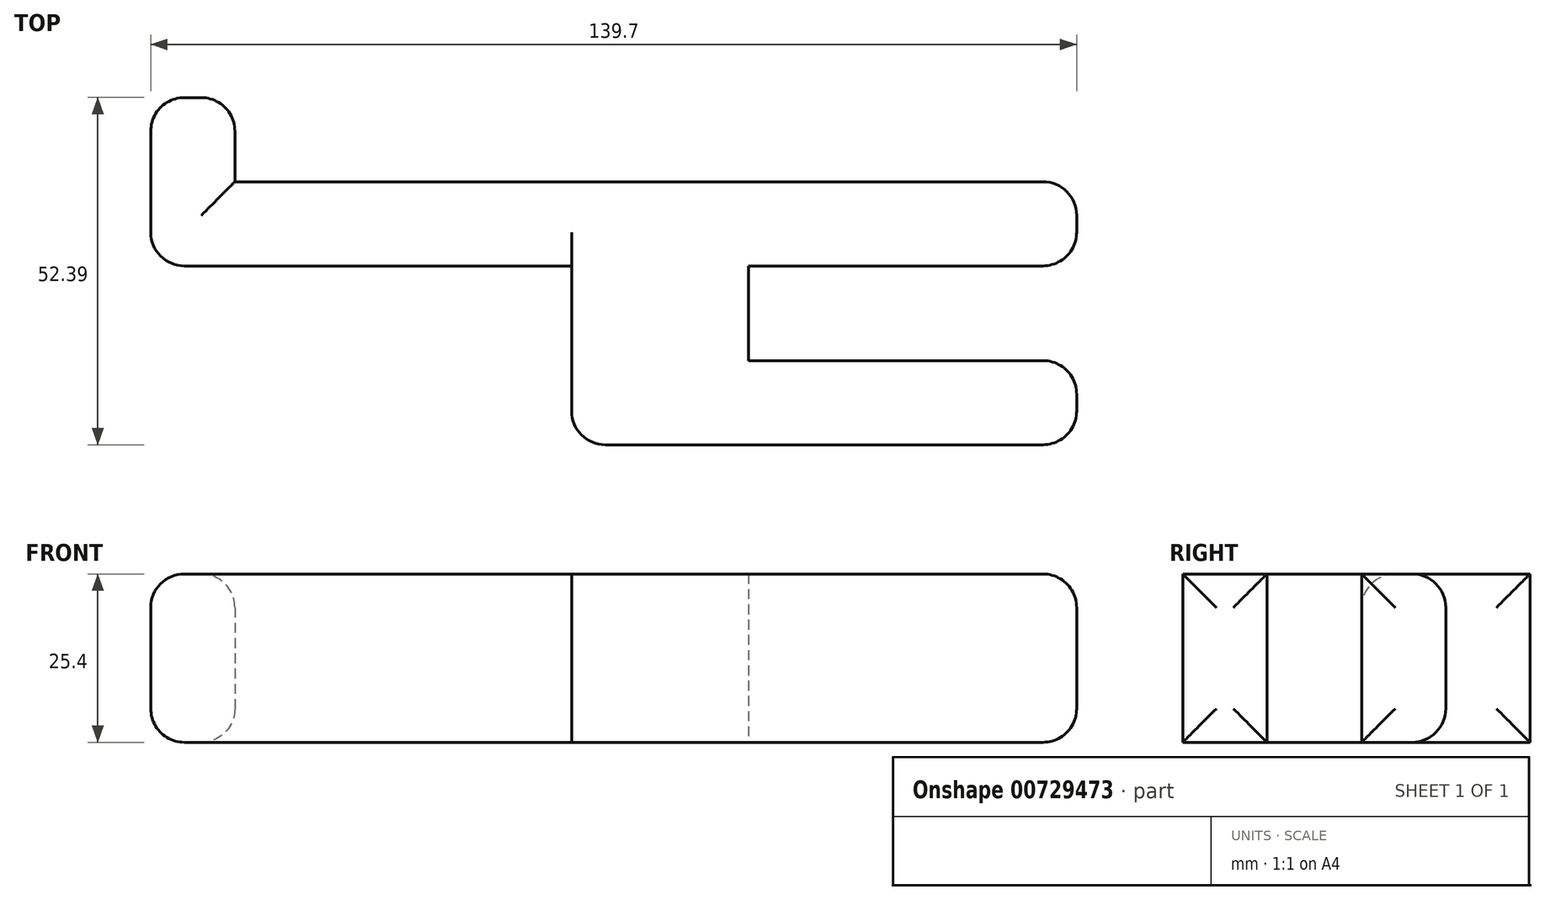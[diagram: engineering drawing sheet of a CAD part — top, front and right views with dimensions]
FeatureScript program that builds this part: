
annotation { "Feature Type Name" : "Feature", "Feature Type Description" : "" }
export const myFeature = defineFeature(function(context is Context, id is Id, definition is map)
    precondition{}
    {
        {
            var Q0;
            Q0=qCreatedBy(makeId("Top.planeOp"),FACE);
            var sketch = newSketch(context, id + "F0", { "sketchPlane" : qUnion([Q0])});
            skLineSegment(sketch, "E0", {"start": v(0, 0) * mm, "end": v(49.52, 0) * mm});
            skLineSegment(sketch, "E1", {"start": v(0, 0) * mm, "end": v(0, 14.29) * mm});
            skLineSegment(sketch, "E2", {"start": v(49.52, 14.29) * mm, "end": v(0, 14.29) * mm});
            skLineSegment(sketch, "E3", {"start": v(49.52, 0) * mm, "end": v(49.52, -12.7) * mm});
            skLineSegment(sketch, "E4", {"start": v(49.52, -12.7) * mm, "end": v(-26.68, -12.7) * mm});
            skLineSegment(sketch, "E5", {"start": v(49.52, 14.29) * mm, "end": v(49.52, 26.99) * mm});
            skLineSegment(sketch, "E6", {"start": v(49.52, 26.99) * mm, "end": v(-77.48, 26.99) * mm});
            skLineSegment(sketch, "E7", {"start": v(-77.48, 26.99) * mm, "end": v(-77.48, 39.69) * mm});
            skLineSegment(sketch, "E8", {"start": v(-77.48, 39.69) * mm, "end": v(-90.18, 39.69) * mm});
            skLineSegment(sketch, "E9", {"start": v(-90.18, 39.69) * mm, "end": v(-90.18, 14.29) * mm});
            skLineSegment(sketch, "E10", {"start": v(-90.18, 14.29) * mm, "end": v(-26.68, 14.29) * mm});
            skLineSegment(sketch, "E11", {"start": v(-26.68, 14.29) * mm, "end": v(-26.68, -12.7) * mm});
            skSolve(sketch);
        }
        {
            var Q0;
            Q0=makeQuery(id+"F0.imprint","IMPRINT",FACE,{"disambiguationData":[TD([[makeQuery(id+"F0.imprint","IMPRINT",EDGE,{"derivedFrom":sQuery(id+"F0.wireOp",EDGE,"E0")}),-1.0]])]});
            extrude(context, id + "F1", {"entities" : qUnion([Q0]), "depth" : 25.4 * mm, "offsetDistance" : 25.4 * mm});
        }
        {
            var Q0;
            Q0=makeQuery(id+"F1.opExtrude","SWEPT_FACE",FACE,{"disambiguationData":[OSD([sQuery(id+"F0.wireOp",EDGE,"E5")])]});
            var Q1;
            Q1=makeQuery(id+"F1.opExtrude","SWEPT_FACE",FACE,{"disambiguationData":[OSD([sQuery(id+"F0.wireOp",EDGE,"E3")])]});
            var Q2;
            Q2=makeQuery(id+"F1.opExtrude","CAP_EDGE",EDGE,{"disambiguationData":[OSD([sQuery(id+"F0.wireOp",EDGE,"E6")])],"isStart":false});
            var Q3;
            Q3=makeQuery(id+"F1.opExtrude","CAP_EDGE",EDGE,{"disambiguationData":[OSD([sQuery(id+"F0.wireOp",EDGE,"E10")])],"isStart":false});
            var Q4;
            Q4=makeQuery(id+"F1.opExtrude","CAP_EDGE",EDGE,{"disambiguationData":[OSD([sQuery(id+"F0.wireOp",EDGE,"E7")])],"isStart":false});
            var Q5;
            Q5=makeQuery(id+"F1.opExtrude","CAP_EDGE",EDGE,{"disambiguationData":[OSD([sQuery(id+"F0.wireOp",EDGE,"E7")])],"isStart":true});
            var Q6;
            Q6=makeQuery(id+"F1.opExtrude","CAP_EDGE",EDGE,{"disambiguationData":[OSD([sQuery(id+"F0.wireOp",EDGE,"E6")])],"isStart":true});
            var Q7;
            Q7=makeQuery(id+"F1.opExtrude","SWEPT_EDGE",EDGE,{"disambiguationData":[OSD([sQuery(id+"F0.wireOp",EDGE,"E7"),sQuery(id+"F0.wireOp",EDGE,"E8")])]});
            var Q8;
            Q8=makeQuery(id+"F1.opExtrude","SWEPT_FACE",FACE,{"disambiguationData":[OSD([sQuery(id+"F0.wireOp",EDGE,"E9")])]});
            var Q9;
            Q9=makeQuery(id+"F1.opExtrude","SWEPT_EDGE",EDGE,{"disambiguationData":[OSD([sQuery(id+"F0.wireOp",EDGE,"E4"),sQuery(id+"F0.wireOp",EDGE,"E11")])]});
            fillet(context, id + "F2", {"entities" : qUnion([Q0, Q1, Q2, Q3, Q4, Q5, Q6, Q7, Q8, Q9]), "radius" : 5.08 * mm, "tangentPropagation" : true, "allowEdgeOverflow" : false});
        }
    });
